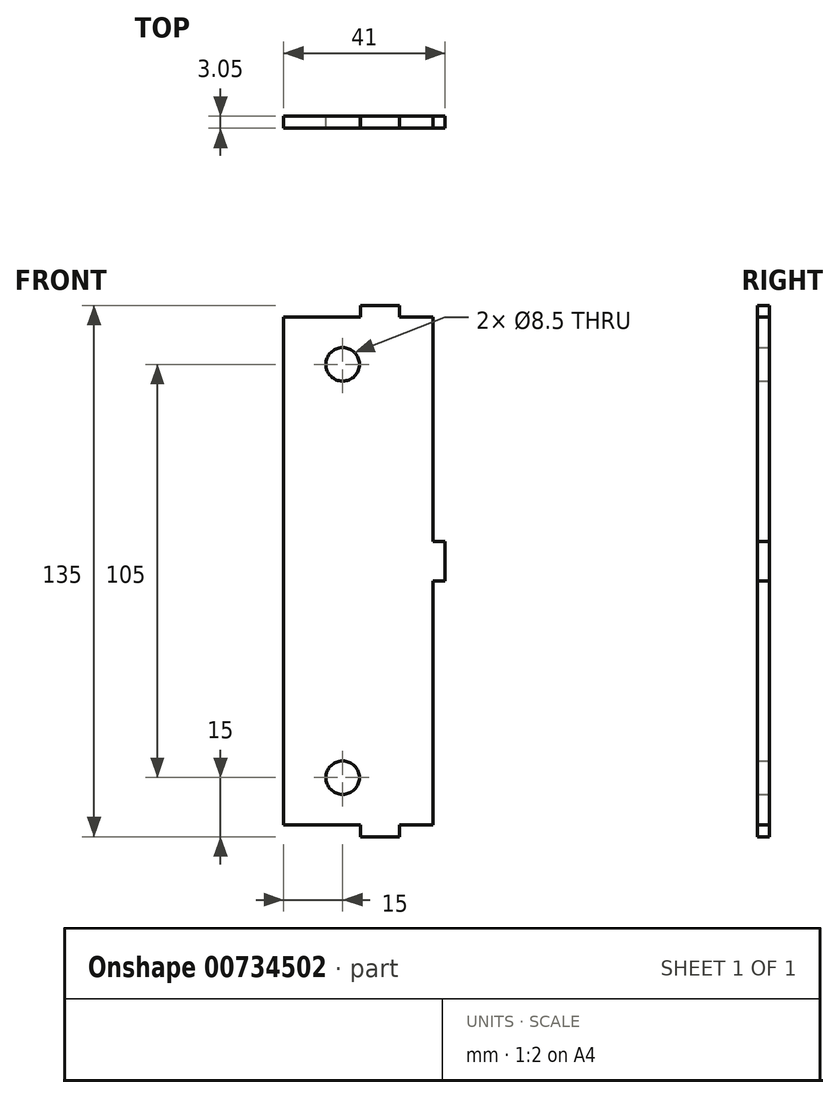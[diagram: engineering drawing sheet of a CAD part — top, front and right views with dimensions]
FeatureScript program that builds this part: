
annotation { "Feature Type Name" : "Feature", "Feature Type Description" : "" }
export const myFeature = defineFeature(function(context is Context, id is Id, definition is map)
    precondition{}
    {
        {
            var Q0;
            Q0=qCreatedBy(makeId("Front.planeOp"),FACE);
            var sketch = newSketch(context, id + "F0", { "sketchPlane" : qUnion([Q0])});
            skLineSegment(sketch, "E0", {"start": v(17.5, -2.5) * mm, "end": v(17.5, -64.5) * mm});
            skLineSegment(sketch, "E1", {"start": v(17.5, -64.5) * mm, "end": v(9, -64.5) * mm});
            skLineSegment(sketch, "E2", {"start": v(9, -64.5) * mm, "end": v(9, -67.5) * mm});
            skLineSegment(sketch, "E3", {"start": v(9, -67.5) * mm, "end": v(-1, -67.5) * mm});
            skLineSegment(sketch, "E4", {"start": v(-1, -67.5) * mm, "end": v(-1, -64.5) * mm});
            skLineSegment(sketch, "E5", {"start": v(-1, -64.5) * mm, "end": v(-20.5, -64.5) * mm});
            skLineSegment(sketch, "E6", {"start": v(-20.5, -64.5) * mm, "end": v(-20.5, 64.5) * mm});
            skLineSegment(sketch, "E7", {"start": v(-20.5, 64.5) * mm, "end": v(-1, 64.5) * mm});
            skLineSegment(sketch, "E8", {"start": v(-1, 64.5) * mm, "end": v(-1, 67.5) * mm});
            skLineSegment(sketch, "E9", {"start": v(-1, 67.5) * mm, "end": v(9, 67.5) * mm});
            skLineSegment(sketch, "E10", {"start": v(9, 67.5) * mm, "end": v(9, 64.5) * mm});
            skLineSegment(sketch, "E11", {"start": v(9, 64.5) * mm, "end": v(17.5, 64.5) * mm});
            skLineSegment(sketch, "E12", {"start": v(17.5, 64.5) * mm, "end": v(17.5, 7.5) * mm});
            skLineSegment(sketch, "E13", {"start": v(17.5, 7.5) * mm, "end": v(20.5, 7.5) * mm});
            skLineSegment(sketch, "E14", {"start": v(20.5, 7.5) * mm, "end": v(20.5, -2.5) * mm});
            skLineSegment(sketch, "E15", {"start": v(20.5, -2.5) * mm, "end": v(17.5, -2.5) * mm});
            skCircle(sketch, "E16", {"center": v(-5.5, -52.5) * mm, "radius": 4.25 * mm});
            skCircle(sketch, "E17", {"center": v(-5.5, 52.5) * mm, "radius": 4.25 * mm});
            skSolve(sketch);
        }
        {
            var Q0;
            Q0 = qSketchRegion(id + "F0", true);
            extrude(context, id + "F1", {"entities" : qUnion([Q0]), "depth" : 3.05 * mm, "offsetDistance" : 25.4 * mm});
        }
    });
